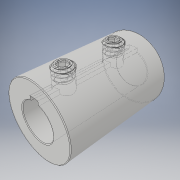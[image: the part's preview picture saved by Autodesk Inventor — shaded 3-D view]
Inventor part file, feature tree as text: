
AUTODESK INVENTOR PART (.ipt)
format: ipt  version: 2019 (Build 230136000, 136)  size: 542,208 bytes
history: native  units: in
note: dims shown in document units (in); Inventor stores cm internally (conversion verified against a paired STEP export)
features: other x2, fillet x1
ambient origin geometry x8: Origin, YZ Plane, XZ Plane, XY Plane, X Axis, Y Axis, Z Axis, Center Point
bodies: Solid1 (feature_tree), Solid2 (feature_tree), Solid3 (feature_tree)
feature tree (3):
  other  "Cut-Extrude3"
  other  "LPattern1"
  fillet  "Fillet1"  [1 undecoded]
note: 1 required parameter value undecoded (feature->parameter linkage not recoverable at this tier; creation-order binding heuristic only, values carry confidence <= 0.55)
